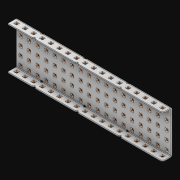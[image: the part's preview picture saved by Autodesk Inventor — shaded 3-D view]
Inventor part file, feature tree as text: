
AUTODESK INVENTOR PART (.ipt)
format: ipt  version: 2021 (Build 250183000, 183)  size: 3,323,392 bytes
history: native  units: in
note: dims shown in document units (in); Inventor stores cm internally (conversion verified against a paired STEP export)
features: extrude x127, other x126, sketch x4, thicken_offset x3, pattern_linear x3, imported_body x1
ambient origin geometry x8: Origin, YZ Plane, XZ Plane, XY Plane, X Axis, Y Axis, Z Axis, Center Point
bodies: Solid1 (feature_tree)
feature tree (264):
  thicken_offset  "Thicken1"
  thicken_offset  "Thicken2"
  thicken_offset  "Thicken3"
  pattern_linear  "Rectangular Pattern1"  Spacing1=0.001in  [1 undecoded]
  pattern_linear  "Rectangular Pattern2"  Spacing1=0.001in  [1 undecoded]
  pattern_linear  "Rectangular Pattern3"  Spacing1=0.182in  [1 undecoded]
  extrude  "Extrusion1"  Depth=0.063in TaperAngle=0.0deg
  sketch  "Sketch1"  dims[d0=0.001in]
  other  "Srf1"
  sketch  "Sketch2"  dims[d1=0.001in]
  other  "Srf2"
  sketch  "Sketch3"  dims[d2=0.001in]
  other  "Srf3"
  other  "Srf4"
  other  "Srf5"
  other  "Srf6"
  other  "Srf7"
  other  "Srf8"
  other  "Srf9"
  other  "Srf10"
  other  "Srf11"
  other  "Srf12"
  other  "Srf13"
  other  "Srf14"
  other  "Srf15"
  other  "Srf16"
  other  "Srf17"
  other  "Srf18"
  other  "Srf19"
  other  "Srf20"
  other  "Srf38"
  other  "Srf39"
  other  "Srf40"
  other  "Srf41"
  other  "Srf42"
  other  "Srf43"
  other  "Srf44"
  other  "Srf45"
  other  "Srf46"
  other  "Srf47"
  other  "Srf48"
  other  "Srf49"
  other  "Srf50"
  other  "Srf51"
  other  "Srf52"
  other  "Srf53"
  other  "Srf54"
  other  "Srf72"
  other  "Srf73"
  other  "Srf74"
  other  "Srf75"
  other  "Srf76"
  other  "Srf77"
  other  "Srf78"
  other  "Srf79"
  other  "Srf80"
  other  "Srf81"
  other  "Srf82"
  other  "Srf83"
  other  "Srf84"
  other  "Srf85"
  other  "Srf86"
  other  "Srf87"
  other  "Srf88"
  other  "Srf106"
  other  "Srf107"
  other  "Srf108"
  other  "Srf109"
  other  "Srf110"
  other  "Srf111"
  other  "Srf112"
  other  "Srf113"
  other  "Srf114"
  other  "Srf115"
  other  "Srf116"
  other  "Srf117"
  other  "Srf118"
  other  "Srf119"
  other  "Srf120"
  other  "Srf121"
  other  "Srf122"
  other  "Srf123"
  other  "Srf141"
  other  "Srf142"
  other  "Srf143"
  other  "Srf144"
  other  "Srf145"
  other  "Srf146"
  other  "Srf147"
  other  "Srf148"
  other  "Srf149"
  other  "Srf150"
  other  "Srf151"
  other  "Srf152"
  other  "Srf153"
  other  "Srf154"
  other  "Srf155"
  other  "Srf156"
  other  "Srf157"
  other  "Srf158"
  other  "Srf176"
  other  "Srf177"
  other  "Srf178"
  other  "Srf179"
  other  "Srf180"
  other  "Srf181"
  other  "Srf182"
  other  "Srf183"
  other  "Srf184"
  other  "Srf185"
  other  "Srf186"
  other  "Srf187"
  other  "Srf188"
  other  "Srf189"
  other  "Srf190"
  other  "Srf191"
  other  "Srf192"
  other  "Srf193"
  other  "Srf211"
  other  "Srf212"
  other  "Srf213"
  other  "Srf214"
  other  "Srf215"
  other  "Srf216"
  other  "Srf217"
  other  "Srf218"
  other  "Srf219"
  other  "Srf220"
  other  "Srf221"
  other  "Srf222"
  other  "Srf223"
  other  "Srf224"
  other  "Srf225"
  other  "Srf226"
  other  "Srf227"
  other  "Srf228"
  sketch  "Sketch4"  dims[d3=0.001in d4=0.001in d5=0.001in d6=0.182in d7=0.063in d8=0.0in d9=0.182in d10=0.063in d11=0.0in d12=0.182in d13=0.063in d14=0.0in d17=0.5in d18=7.0866in d20=0.5in d21=7.0866in d23=0.5in d24=1.9685in d26=0.5in d27=8.5in d28=0.0in]
  imported_body  "Imported1"
  extrude  "ExtrusionSrf1"  Depth=8.5in
  extrude  "ExtrusionSrf2"  Depth=0.063in TaperAngle=0.0deg
  extrude  "ExtrusionSrf3"  Depth=8.5in
  extrude  "ExtrusionSrf4"  Depth=0.063in TaperAngle=0.0deg
  extrude  "ExtrusionSrf5"  Depth=0.5in
  extrude  "ExtrusionSrf6"  Depth=8.5in
  extrude  "ExtrusionSrf7"  Depth=0.5in
  extrude  "ExtrusionSrf8"  Depth=8.5in
  extrude  "ExtrusionSrf9"  Depth=0.5in
  extrude  "ExtrusionSrf10"  Depth=0.5in
  extrude  "ExtrusionSrf11"  Depth=8.5in
  extrude  "ExtrusionSrf12"  TaperAngle=0.0deg  [1 undecoded]
  extrude  "ExtrusionSrf13"  [1 undecoded]
  extrude  "ExtrusionSrf14"  [1 undecoded]
  extrude  "ExtrusionSrf15"  [1 undecoded]
  extrude  "ExtrusionSrf16"  [1 undecoded]
  extrude  "ExtrusionSrf17"  [1 undecoded]
  extrude  "ExtrusionSrf18"  [1 undecoded]
  extrude  "ExtrusionSrf19"  [1 undecoded]
  extrude  "ExtrusionSrf20"  [1 undecoded]
  extrude  "ExtrusionSrf38"  [1 undecoded]
  extrude  "ExtrusionSrf39"  [1 undecoded]
  extrude  "ExtrusionSrf40"  [1 undecoded]
  extrude  "ExtrusionSrf41"  [1 undecoded]
  extrude  "ExtrusionSrf42"  [1 undecoded]
  extrude  "ExtrusionSrf43"  [1 undecoded]
  extrude  "ExtrusionSrf44"  [1 undecoded]
  extrude  "ExtrusionSrf45"  [1 undecoded]
  extrude  "ExtrusionSrf46"  [1 undecoded]
  extrude  "ExtrusionSrf47"  [1 undecoded]
  extrude  "ExtrusionSrf48"  [1 undecoded]
  extrude  "ExtrusionSrf49"  [1 undecoded]
  extrude  "ExtrusionSrf50"  [1 undecoded]
  extrude  "ExtrusionSrf51"  [1 undecoded]
  extrude  "ExtrusionSrf52"  [1 undecoded]
  extrude  "ExtrusionSrf53"  [1 undecoded]
  extrude  "ExtrusionSrf54"  [1 undecoded]
  extrude  "ExtrusionSrf72"  [1 undecoded]
  extrude  "ExtrusionSrf73"  [1 undecoded]
  extrude  "ExtrusionSrf74"  [1 undecoded]
  extrude  "ExtrusionSrf75"  [1 undecoded]
  extrude  "ExtrusionSrf76"  [1 undecoded]
  extrude  "ExtrusionSrf77"  [1 undecoded]
  extrude  "ExtrusionSrf78"  [1 undecoded]
  extrude  "ExtrusionSrf79"  [1 undecoded]
  extrude  "ExtrusionSrf80"  [1 undecoded]
  extrude  "ExtrusionSrf81"  [1 undecoded]
  extrude  "ExtrusionSrf82"  [1 undecoded]
  extrude  "ExtrusionSrf83"  [1 undecoded]
  extrude  "ExtrusionSrf84"  [1 undecoded]
  extrude  "ExtrusionSrf85"  [1 undecoded]
  extrude  "ExtrusionSrf86"  [1 undecoded]
  extrude  "ExtrusionSrf87"  [1 undecoded]
  extrude  "ExtrusionSrf88"  [1 undecoded]
  extrude  "ExtrusionSrf106"  [1 undecoded]
  extrude  "ExtrusionSrf107"  [1 undecoded]
  extrude  "ExtrusionSrf108"  [1 undecoded]
  extrude  "ExtrusionSrf109"  [1 undecoded]
  extrude  "ExtrusionSrf110"  [1 undecoded]
  extrude  "ExtrusionSrf111"  [1 undecoded]
  extrude  "ExtrusionSrf112"  [1 undecoded]
  extrude  "ExtrusionSrf113"  [1 undecoded]
  extrude  "ExtrusionSrf114"  [1 undecoded]
  extrude  "ExtrusionSrf115"  [1 undecoded]
  extrude  "ExtrusionSrf116"  [1 undecoded]
  extrude  "ExtrusionSrf117"  [1 undecoded]
  extrude  "ExtrusionSrf118"  [1 undecoded]
  extrude  "ExtrusionSrf119"  [1 undecoded]
  extrude  "ExtrusionSrf120"  [1 undecoded]
  extrude  "ExtrusionSrf121"  [1 undecoded]
  extrude  "ExtrusionSrf122"  [1 undecoded]
  extrude  "ExtrusionSrf123"  [1 undecoded]
  extrude  "ExtrusionSrf141"  [1 undecoded]
  extrude  "ExtrusionSrf142"  [1 undecoded]
  extrude  "ExtrusionSrf143"  [1 undecoded]
  extrude  "ExtrusionSrf144"  [1 undecoded]
  extrude  "ExtrusionSrf145"  [1 undecoded]
  extrude  "ExtrusionSrf146"  [1 undecoded]
  extrude  "ExtrusionSrf147"  [1 undecoded]
  extrude  "ExtrusionSrf148"  [1 undecoded]
  extrude  "ExtrusionSrf149"  [1 undecoded]
  extrude  "ExtrusionSrf150"  [1 undecoded]
  extrude  "ExtrusionSrf151"  [1 undecoded]
  extrude  "ExtrusionSrf152"  [1 undecoded]
  extrude  "ExtrusionSrf153"  [1 undecoded]
  extrude  "ExtrusionSrf154"  [1 undecoded]
  extrude  "ExtrusionSrf155"  [1 undecoded]
  extrude  "ExtrusionSrf156"  [1 undecoded]
  extrude  "ExtrusionSrf157"  [1 undecoded]
  extrude  "ExtrusionSrf158"  [1 undecoded]
  extrude  "ExtrusionSrf176"  [1 undecoded]
  extrude  "ExtrusionSrf177"  [1 undecoded]
  extrude  "ExtrusionSrf178"  [1 undecoded]
  extrude  "ExtrusionSrf179"  [1 undecoded]
  extrude  "ExtrusionSrf180"  [1 undecoded]
  extrude  "ExtrusionSrf181"  [1 undecoded]
  extrude  "ExtrusionSrf182"  [1 undecoded]
  extrude  "ExtrusionSrf183"  [1 undecoded]
  extrude  "ExtrusionSrf184"  [1 undecoded]
  extrude  "ExtrusionSrf185"  [1 undecoded]
  extrude  "ExtrusionSrf186"  [1 undecoded]
  extrude  "ExtrusionSrf187"  [1 undecoded]
  extrude  "ExtrusionSrf188"  [1 undecoded]
  extrude  "ExtrusionSrf189"  [1 undecoded]
  extrude  "ExtrusionSrf190"  [1 undecoded]
  extrude  "ExtrusionSrf191"  [1 undecoded]
  extrude  "ExtrusionSrf192"  [1 undecoded]
  extrude  "ExtrusionSrf193"  [1 undecoded]
  extrude  "ExtrusionSrf211"  [1 undecoded]
  extrude  "ExtrusionSrf212"  [1 undecoded]
  extrude  "ExtrusionSrf213"  [1 undecoded]
  extrude  "ExtrusionSrf214"  [1 undecoded]
  extrude  "ExtrusionSrf215"  [1 undecoded]
  extrude  "ExtrusionSrf216"  [1 undecoded]
  extrude  "ExtrusionSrf217"  [1 undecoded]
  extrude  "ExtrusionSrf218"  [1 undecoded]
  extrude  "ExtrusionSrf219"  [1 undecoded]
  extrude  "ExtrusionSrf220"  [1 undecoded]
  extrude  "ExtrusionSrf221"  [1 undecoded]
  extrude  "ExtrusionSrf222"  [1 undecoded]
  extrude  "ExtrusionSrf223"  [1 undecoded]
  extrude  "ExtrusionSrf224"  [1 undecoded]
  extrude  "ExtrusionSrf225"  [1 undecoded]
  extrude  "ExtrusionSrf226"  [1 undecoded]
  extrude  "ExtrusionSrf227"  [1 undecoded]
  extrude  "ExtrusionSrf228"  [1 undecoded]
note: 118 required parameter values undecoded (feature->parameter linkage not recoverable at this tier; creation-order binding heuristic only, values carry confidence <= 0.55)
